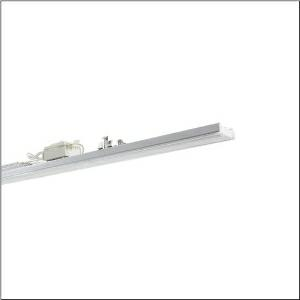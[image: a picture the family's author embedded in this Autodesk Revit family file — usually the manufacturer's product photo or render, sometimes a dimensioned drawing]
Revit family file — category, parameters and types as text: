
# Revit family: licross_21_recessed_mo_52tl1emn4a5g
name_source: partatom
category: Lighting Fixtures
units: mm (PartAtom-declared; Revit-internal decimal feet)

## family parameters
Cut with Voids When Loaded = No
Host = Face
Light Source = No
Part Type = Normal
Room Calculation Point = No
Round Connector Dimension = Use Diameter
Shared = No

## types (1)
- --- (1 x LED, 10630 lm, 60.5 W, 4000K)
    Apparent Load = 61 VA
    CIE Flux Codes = 85 95 99 100 100
    Color Rendering = 80
    Color Temperature = 4000K
    Default Elevation = 1800 mm
    Description = Licross 21 Recessed MO, luminaire insert, of sheet steel, galvanised, coil coated, white, length: 1.500mm, width: 66mm, height: 67mm, LED rated luminous flux: 10.630lm, light colour: 840, SDCM (Standard Deviation of Colour Matching)MacAdam ≤ 3 SDCM (initial), control gear: ON/OFF Multilumen, with plug, 3-pole, with phase selection, mains connection: 220..240V, AC, 50/60Hz, rated input power: 61W, internal wiring halogen-free, primary light control with lens, of plastic, primary optical cover: cover, of PMMA, light emission: direct distribution, primary light characteristic: symmetric, protection rating (complete): IP40, insulation class (complete): insulation class I (protective earthing), certification: CE, ENEC, VDE, UKCA, protection symbol: D if used in an environment without relevant dust loads with corresponding accessories, impact resistance: IK06, permissible ambient temperature for indoor applications: -35..+40°C, corresponds to IFS (International Featured Standards) requirements for safety and quality in the food industry, reducing of maximum allowable ambient temperature of 5°C with ceiling mounting, LABS conformity tested according to VDMA 24364:2018-05, The light source and the operating device comply with the requirements of the Ecodesign Regulation (EU) 2019/2020 and are replaceable in accordance with this regulation, packaging unit: 1 piece
    Height = 58 mm
    Lamp = 1 x LED
    Lamp Light Flux = 10630 lm
    Lamp Power = 60.5 W
    Lamp count = 1
    Length = 1500 mm
    Luminous efficacy = 176 lm/W
    Manufacturer = Siteco
    ModVariant = No
    Model = 52TL1EMN4A5G
    Mounting Place = Ceiling
    Mounting Type = Pendant
    Number of Poles = 1
    OnlyDefault = Yes
    Power Factor = 1
    Product Name = Licross 21 Recessed MO
    Product group = luminaire insert | ceiling pendant
    ProductGroupID = 901
    Protection Class = Protection class I
    Protection Degree = IP 40
    RLX_Detail_Level = 1
    RLX_Emergency_Light_Flux = 0 lm
    RLX_Emergency_Type = 0
    RLX_Emergency_Type_DB = No
    RlxData = <blob elided: 22609 chars, md5=c05e0b3e>
    Socket = socket
    Standby Power = 0 W
    System Light Flux = 10630 lm
    System Power = 61 W
    Type Comments = factory setting: luminous flux: 100 % | (A | C | E) | 140 mA
    Type Image = l_1296930.jpg
    URL = http://relux.com
    VarID = @adj_106455
    Voltage = 0 V
    Weight = 0.00 kg
    Width = 66 mm

## geometry (parser evidence)
native form markers: Blend x4, Sweep x11
no freeform markers — native parametric forms only
